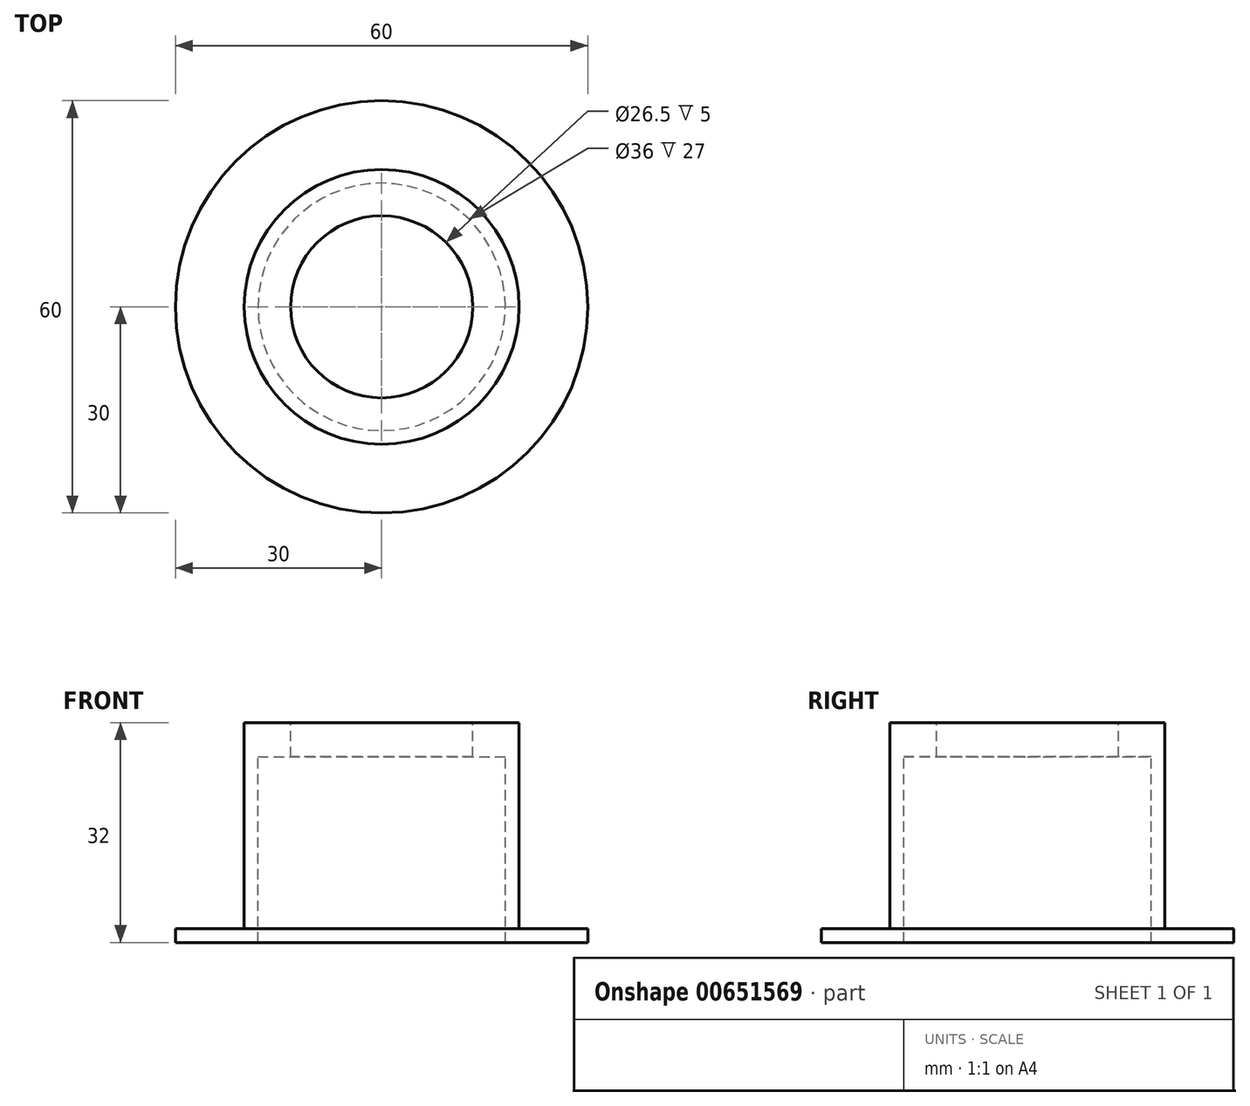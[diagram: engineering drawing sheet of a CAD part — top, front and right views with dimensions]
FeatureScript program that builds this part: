
annotation { "Feature Type Name" : "Feature", "Feature Type Description" : "" }
export const myFeature = defineFeature(function(context is Context, id is Id, definition is map)
    precondition{}
    {
        {
            var Q0;
            Q0=qCreatedBy(makeId("Top.planeOp"),FACE);
            var sketch = newSketch(context, id + "F0", { "sketchPlane" : qUnion([Q0])});
            skCircle(sketch, "E0", {"center": v(0, 0) * mm, "radius": 20 * mm});
            skCircle(sketch, "E1", {"center": v(0, 0) * mm, "radius": 13.25 * mm});
            skSolve(sketch);
        }
        {
            var Q0;
            Q0 = qSketchRegion(id + "F0", true);
            extrude(context, id + "F1", {"entities" : qUnion([Q0]), "oppositeDirection" : true, "depth" : 5 * mm, "offsetDistance" : 25 * mm});
        }
        {
            var Q0;
            Q0=makeQuery(id+"F1.opExtrude","CAP_FACE",FACE,{"disambiguationData":[OSD([sQuery(id+"F0.wireOp",EDGE,"E0"),sQuery(id+"F0.wireOp",EDGE,"E1")])],"isStart":false});
            var sketch = newSketch(context, id + "F2", { "sketchPlane" : qUnion([Q0])});
            skCircle(sketch, "E2", {"center": v(0, 0) * mm, "radius": 20 * mm});
            skCircle(sketch, "E3.0", {"center": v(0, 0) * mm, "radius": 18 * mm});
            skSolve(sketch);
        }
        {
            var Q0;
            Q0=makeQuery(id+"F2.imprint","IMPRINT",FACE,{"disambiguationData":[TD([[makeQuery(id+"F2.imprint","IMPRINT",EDGE,{"derivedFrom":sQuery(id+"F2.wireOp",EDGE,"E2")}),-1.0]])]});
            extrude(context, id + "F3", {"entities" : qUnion([Q0]), "operationType" : NewBodyOperationType.ADD, "depth" : 25 * mm, "offsetDistance" : 25 * mm});
        }
        {
            var Q0;
            Q0=makeQuery(id+"F3.opExtrude","CAP_FACE",FACE,{"disambiguationData":[OSD([sQuery(id+"F2.wireOp",EDGE,"E2"),sQuery(id+"F2.wireOp",EDGE,"E3.0")])],"isStart":false});
            var sketch = newSketch(context, id + "F4", { "sketchPlane" : qUnion([Q0])});
            skCircle(sketch, "E4", {"center": v(0, 0) * mm, "radius": 18 * mm});
            skCircle(sketch, "E5", {"center": v(0, 0) * mm, "radius": 30 * mm});
            skSolve(sketch);
        }
        {
            var Q0;
            Q0 = qSketchRegion(id + "F4", true);
            extrude(context, id + "F5", {"entities" : qUnion([Q0]), "operationType" : NewBodyOperationType.ADD, "depth" : 2 * mm, "offsetDistance" : 25 * mm});
        }
    });
